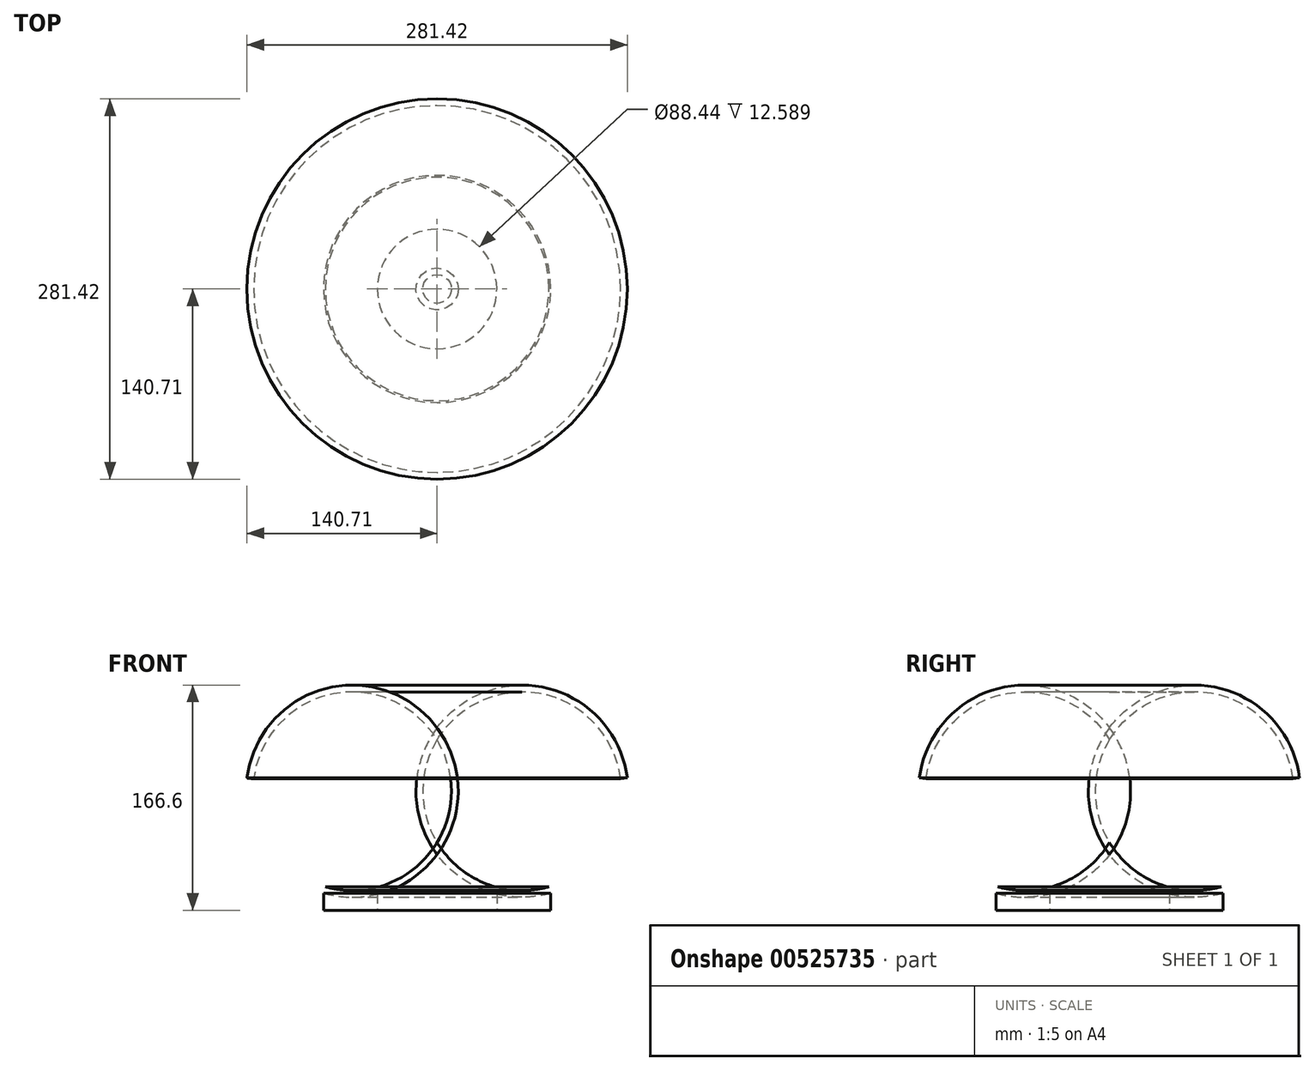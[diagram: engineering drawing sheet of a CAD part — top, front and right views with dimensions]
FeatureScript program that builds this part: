
annotation { "Feature Type Name" : "Feature", "Feature Type Description" : "" }
export const myFeature = defineFeature(function(context is Context, id is Id, definition is map)
    precondition{}
    {
        {
            var Q0;
            Q0=qCreatedBy(makeId("Front.planeOp"),FACE);
            var sketch = newSketch(context, id + "F0", { "sketchPlane" : qUnion([Q0])});
            skLineSegment(sketch, "E0", {"start": v(0, 0) * mm, "end": v(0, 171.43) * mm, "construction": true});
            skLineSegment(sketch, "E1", {"start": v(0, 12.59) * mm, "end": v(44.22, 12.59) * mm});
            skLineSegment(sketch, "E2", {"start": v(44.22, 12.59) * mm, "end": v(44.22, 0) * mm});
            skLineSegment(sketch, "E3", {"start": v(44.22, 0) * mm, "end": v(84.06, 0) * mm});
            skLineSegment(sketch, "E4", {"start": v(84.06, 0) * mm, "end": v(84.06, 12.59) * mm});
            skArc(sketch, "E5", {"start": v(84.06, 12.59) * mm, "mid": v(128.22, 44.72) * mm, "end": v(140.71, 97.88) * mm});
            skArc(sketch, "E6.0", {"start": v(82.71, 17.4) * mm, "mid": v(124.05, 47.49) * mm, "end": v(135.75, 97.26) * mm});
            skLineSegment(sketch, "E7", {"start": v(135.75, 97.26) * mm, "end": v(140.71, 97.88) * mm});
            skLineSegment(sketch, "E8", {"start": v(82.71, 17.4) * mm, "end": v(0, 17.4) * mm});
            skLineSegment(sketch, "E9", {"start": v(0, 17.4) * mm, "end": v(0, 7.6) * mm});
            skSolve(sketch);
        }
        {
            var Q0;
            {var subQ0=sQuery(id+"F0.wireOp",EDGE,"E1");Q0=makeQuery(id+"F0.imprint","IMPRINT",FACE,{"disambiguationData":[TD([[makeQuery(id+"F0.imprint","IMPRINT",EDGE,{"derivedFrom":subQ0}),1.0]])]});}
            var Q1;
            Q1=sQuery(id+"F0.wireOp",EDGE,"E0");
            revolve(context, id + "F1", {"entities" : qUnion([Q0]), "axis" : qUnion([Q1]), "revolveType" : RevolveType.FULL});
        }
    });
